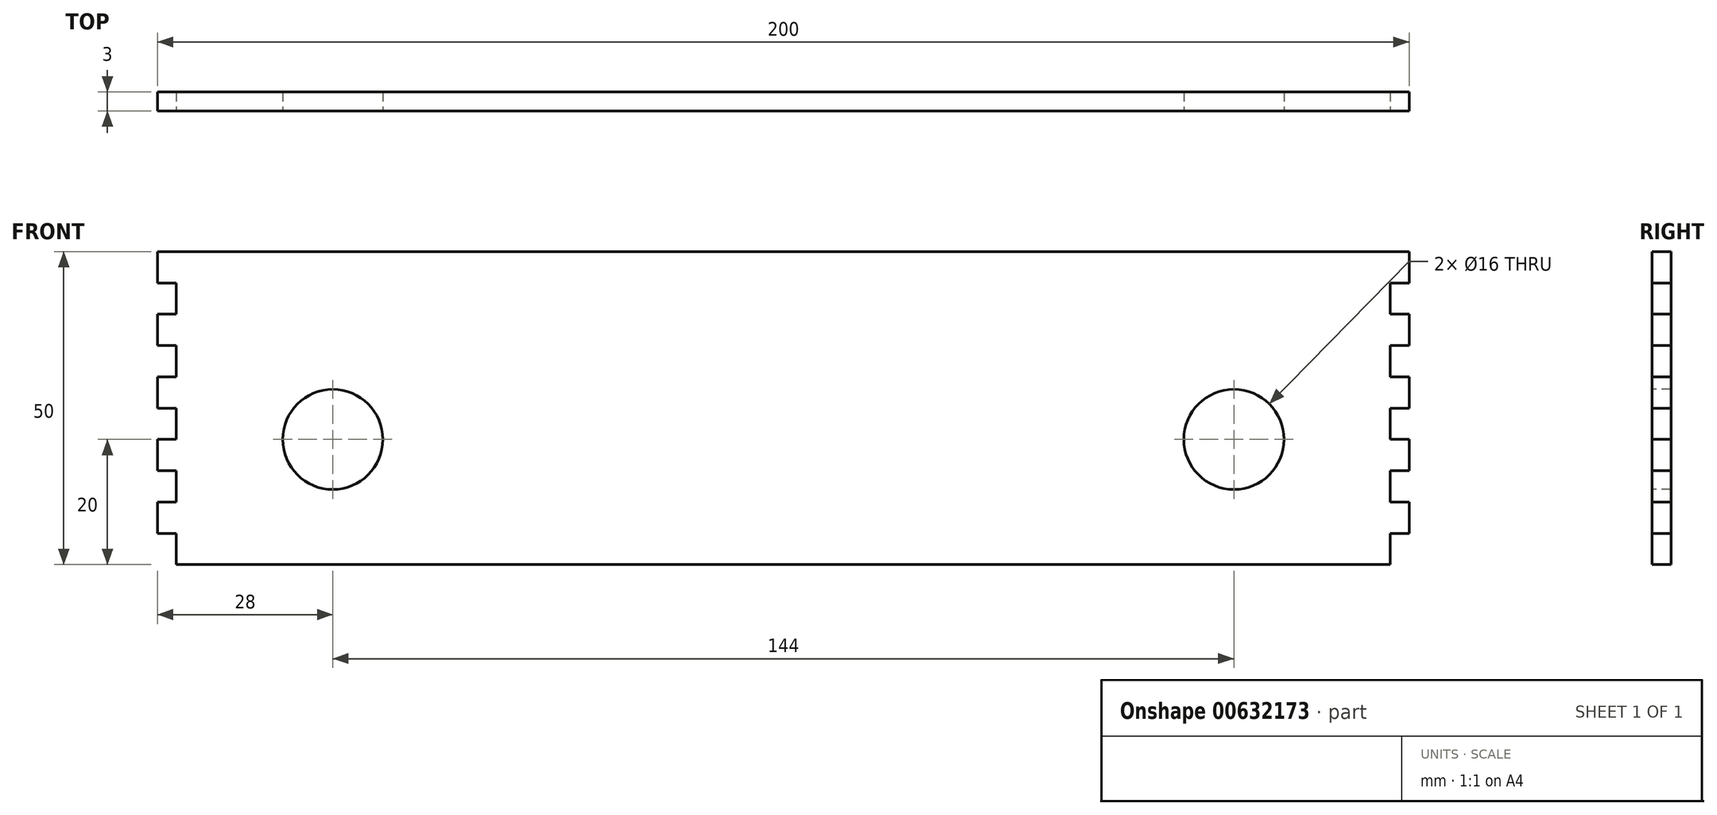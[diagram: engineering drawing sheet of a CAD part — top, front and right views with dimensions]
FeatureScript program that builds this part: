
annotation { "Feature Type Name" : "Feature", "Feature Type Description" : "" }
export const myFeature = defineFeature(function(context is Context, id is Id, definition is map)
    precondition{}
    {
        {
            var Q0;
            Q0=qCreatedBy(makeId("Front.planeOp"),FACE);
            var sketch = newSketch(context, id + "F0", { "sketchPlane" : qUnion([Q0])});
            skLineSegment(sketch, "E0.bottom", {"start": v(97, 25) * mm, "end": v(-97, 25) * mm});
            skLineSegment(sketch, "E0.top", {"start": v(97, -25) * mm, "end": v(-97, -25) * mm});
            skLineSegment(sketch, "E0.left", {"start": v(97, 25) * mm, "end": v(97, -25) * mm});
            skLineSegment(sketch, "E0.right", {"start": v(-97, 25) * mm, "end": v(-97, -25) * mm});
            skPoint(sketch, "E0.middle", {"position": v(0, 0) * mm});
            skSolve(sketch);
        }
        {
            var Q0;
            Q0=makeQuery(id+"F0.imprint","IMPRINT",FACE,{"disambiguationData":[TD([[makeQuery(id+"F0.imprint","IMPRINT",EDGE,{"derivedFrom":sQuery(id+"F0.wireOp",EDGE,"E0.bottom")}),1.0]])]});
            extrude(context, id + "F1", {"entities" : qUnion([Q0]), "depth" : 3 * mm, "offsetDistance" : 25 * mm});
        }
        {
            var Q0;
            Q0=makeQuery(id+"F1.opExtrude","CAP_FACE",FACE,{"disambiguationData":[OSD([sQuery(id+"F0.wireOp",EDGE,"E0.bottom"),sQuery(id+"F0.wireOp",EDGE,"E0.top"),sQuery(id+"F0.wireOp",EDGE,"E0.left"),sQuery(id+"F0.wireOp",EDGE,"E0.right")])],"isStart":false});
            var sketch = newSketch(context, id + "F2", { "sketchPlane" : qUnion([Q0])});
            skLineSegment(sketch, "E1.bottom", {"start": v(-97, 25) * mm, "end": v(-100, 25) * mm});
            skLineSegment(sketch, "E1.top", {"start": v(-97, 20) * mm, "end": v(-100, 20) * mm});
            skLineSegment(sketch, "E1.left", {"start": v(-97, 25) * mm, "end": v(-97, 20) * mm});
            skLineSegment(sketch, "E1.right", {"start": v(-100, 25) * mm, "end": v(-100, 20) * mm});
            skLineSegment(sketch, "E2.0.1.0", {"start": v(-97, 15) * mm, "end": v(-100, 15) * mm});
            skLineSegment(sketch, "E2.0.1.1", {"start": v(-97, 10) * mm, "end": v(-100, 10) * mm});
            skLineSegment(sketch, "E2.0.1.2", {"start": v(-97, 15) * mm, "end": v(-97, 10) * mm});
            skLineSegment(sketch, "E2.0.1.3", {"start": v(-100, 15) * mm, "end": v(-100, 10) * mm});
            skLineSegment(sketch, "E2.0.2.0", {"start": v(-97, 5) * mm, "end": v(-100, 5) * mm});
            skLineSegment(sketch, "E2.0.2.1", {"start": v(-97, 0) * mm, "end": v(-100, 0) * mm});
            skLineSegment(sketch, "E2.0.2.2", {"start": v(-97, 5) * mm, "end": v(-97, 0) * mm});
            skLineSegment(sketch, "E2.0.2.3", {"start": v(-100, 5) * mm, "end": v(-100, 0) * mm});
            skLineSegment(sketch, "E2.0.3.0", {"start": v(-97, -5) * mm, "end": v(-100, -5) * mm});
            skLineSegment(sketch, "E2.0.3.1", {"start": v(-97, -10) * mm, "end": v(-100, -10) * mm});
            skLineSegment(sketch, "E2.0.3.2", {"start": v(-97, -5) * mm, "end": v(-97, -10) * mm});
            skLineSegment(sketch, "E2.0.3.3", {"start": v(-100, -5) * mm, "end": v(-100, -10) * mm});
            skLineSegment(sketch, "E2.0.4.0", {"start": v(-97, -15) * mm, "end": v(-100, -15) * mm});
            skLineSegment(sketch, "E2.0.4.1", {"start": v(-97, -20) * mm, "end": v(-100, -20) * mm});
            skLineSegment(sketch, "E2.0.4.2", {"start": v(-97, -15) * mm, "end": v(-97, -20) * mm});
            skLineSegment(sketch, "E2.0.4.3", {"start": v(-100, -15) * mm, "end": v(-100, -20) * mm});
            skLineSegment(sketch, "E2.direction1", {"start": v(-100, 20) * mm, "end": v(-74.1, 20) * mm, "construction": true});
            skLineSegment(sketch, "E2.direction2", {"start": v(-100, 20) * mm, "end": v(-100, 10) * mm, "construction": true});
            skLineSegment(sketch, "E3.MirrorCS", {"start": v(97, 10) * mm, "end": v(100, 10) * mm});
            skLineSegment(sketch, "E4.MirrorCS", {"start": v(97, 15) * mm, "end": v(100, 15) * mm});
            skLineSegment(sketch, "E5.MirrorCS", {"start": v(100, 15) * mm, "end": v(100, 10) * mm});
            skLineSegment(sketch, "E6.MirrorCS", {"start": v(97, 15) * mm, "end": v(97, 10) * mm});
            skLineSegment(sketch, "E7.MirrorCS", {"start": v(97, 20) * mm, "end": v(100, 20) * mm});
            skLineSegment(sketch, "E8.MirrorCS", {"start": v(100, 20) * mm, "end": v(100, 10) * mm, "construction": true});
            skLineSegment(sketch, "E9.MirrorCS", {"start": v(97, 5) * mm, "end": v(100, 5) * mm});
            skLineSegment(sketch, "E10.MirrorCS", {"start": v(97, 0) * mm, "end": v(100, 0) * mm});
            skLineSegment(sketch, "E11.MirrorCS", {"start": v(100, 25) * mm, "end": v(100, 20) * mm});
            skLineSegment(sketch, "E12.MirrorCS", {"start": v(97, 25) * mm, "end": v(97, 20) * mm});
            skLineSegment(sketch, "E13.MirrorCS", {"start": v(97, 25) * mm, "end": v(100, 25) * mm});
            skLineSegment(sketch, "E14.MirrorCS", {"start": v(97, -10) * mm, "end": v(100, -10) * mm});
            skLineSegment(sketch, "E15.MirrorCS", {"start": v(97, -5) * mm, "end": v(100, -5) * mm});
            skLineSegment(sketch, "E16.MirrorCS", {"start": v(97, 5) * mm, "end": v(97, 0) * mm});
            skLineSegment(sketch, "E17.MirrorCS", {"start": v(100, -5) * mm, "end": v(100, -10) * mm});
            skLineSegment(sketch, "E18.MirrorCS", {"start": v(97, -5) * mm, "end": v(97, -10) * mm});
            skLineSegment(sketch, "E19.MirrorCS", {"start": v(97, -15) * mm, "end": v(100, -15) * mm});
            skLineSegment(sketch, "E20.MirrorCS", {"start": v(100, 5) * mm, "end": v(100, 0) * mm});
            skLineSegment(sketch, "E21.MirrorCS", {"start": v(97, -20) * mm, "end": v(100, -20) * mm});
            skLineSegment(sketch, "E22.MirrorCS", {"start": v(100, -15) * mm, "end": v(100, -20) * mm});
            skLineSegment(sketch, "E23.MirrorCS", {"start": v(97, -15) * mm, "end": v(97, -20) * mm});
            skSolve(sketch);
        }
        {
            var Q0;
            Q0 = qSketchRegion(id + "F2", true);
            extrude(context, id + "F3", {"entities" : qUnion([Q0]), "operationType" : NewBodyOperationType.ADD, "oppositeDirection" : true, "depth" : 3 * mm, "offsetDistance" : 25 * mm});
        }
        {
            var Q0;
            Q0=makeQuery(id+"F3.boolean.opBoolean","MERGE",FACE,{"derivedFrom":[makeQuery(id+"F1.opExtrude","CAP_FACE",FACE,{"disambiguationData":[OSD([sQuery(id+"F0.wireOp",EDGE,"E0.bottom"),sQuery(id+"F0.wireOp",EDGE,"E0.top"),sQuery(id+"F0.wireOp",EDGE,"E0.left"),sQuery(id+"F0.wireOp",EDGE,"E0.right")])],"isStart":false}),makeQuery(id+"F3.opExtrude","CAP_FACE",FACE,{"disambiguationData":[OSD([sQuery(id+"F2.wireOp",EDGE,"E1.bottom"),sQuery(id+"F2.wireOp",EDGE,"E1.top"),sQuery(id+"F2.wireOp",EDGE,"E1.left"),sQuery(id+"F2.wireOp",EDGE,"E1.right")])],"isStart":true}),makeQuery(id+"F3.opExtrude","CAP_FACE",FACE,{"disambiguationData":[OSD([sQuery(id+"F2.wireOp",EDGE,"E2.0.1.0"),sQuery(id+"F2.wireOp",EDGE,"E2.0.1.1"),sQuery(id+"F2.wireOp",EDGE,"E2.0.1.2"),sQuery(id+"F2.wireOp",EDGE,"E2.0.1.3")])],"isStart":true}),makeQuery(id+"F3.opExtrude","CAP_FACE",FACE,{"disambiguationData":[OSD([sQuery(id+"F2.wireOp",EDGE,"E2.0.2.0"),sQuery(id+"F2.wireOp",EDGE,"E2.0.2.1"),sQuery(id+"F2.wireOp",EDGE,"E2.0.2.2"),sQuery(id+"F2.wireOp",EDGE,"E2.0.2.3")])],"isStart":true}),makeQuery(id+"F3.opExtrude","CAP_FACE",FACE,{"disambiguationData":[OSD([sQuery(id+"F2.wireOp",EDGE,"E2.0.3.0"),sQuery(id+"F2.wireOp",EDGE,"E2.0.3.1"),sQuery(id+"F2.wireOp",EDGE,"E2.0.3.2"),sQuery(id+"F2.wireOp",EDGE,"E2.0.3.3")])],"isStart":true}),makeQuery(id+"F3.opExtrude","CAP_FACE",FACE,{"disambiguationData":[OSD([sQuery(id+"F2.wireOp",EDGE,"E2.0.4.0"),sQuery(id+"F2.wireOp",EDGE,"E2.0.4.1"),sQuery(id+"F2.wireOp",EDGE,"E2.0.4.2"),sQuery(id+"F2.wireOp",EDGE,"E2.0.4.3")])],"isStart":true}),makeQuery(id+"F3.opExtrude","CAP_FACE",FACE,{"disambiguationData":[OSD([sQuery(id+"F2.wireOp",EDGE,"E3.MirrorCS"),sQuery(id+"F2.wireOp",EDGE,"E4.MirrorCS"),sQuery(id+"F2.wireOp",EDGE,"E5.MirrorCS"),sQuery(id+"F2.wireOp",EDGE,"E6.MirrorCS")])],"isStart":true}),makeQuery(id+"F3.opExtrude","CAP_FACE",FACE,{"disambiguationData":[OSD([sQuery(id+"F2.wireOp",EDGE,"E7.MirrorCS"),sQuery(id+"F2.wireOp",EDGE,"E11.MirrorCS"),sQuery(id+"F2.wireOp",EDGE,"E12.MirrorCS"),sQuery(id+"F2.wireOp",EDGE,"E13.MirrorCS")])],"isStart":true}),makeQuery(id+"F3.opExtrude","CAP_FACE",FACE,{"disambiguationData":[OSD([sQuery(id+"F2.wireOp",EDGE,"E9.MirrorCS"),sQuery(id+"F2.wireOp",EDGE,"E10.MirrorCS"),sQuery(id+"F2.wireOp",EDGE,"E16.MirrorCS"),sQuery(id+"F2.wireOp",EDGE,"E20.MirrorCS")])],"isStart":true}),makeQuery(id+"F3.opExtrude","CAP_FACE",FACE,{"disambiguationData":[OSD([sQuery(id+"F2.wireOp",EDGE,"E14.MirrorCS"),sQuery(id+"F2.wireOp",EDGE,"E15.MirrorCS"),sQuery(id+"F2.wireOp",EDGE,"E17.MirrorCS"),sQuery(id+"F2.wireOp",EDGE,"E18.MirrorCS")])],"isStart":true}),makeQuery(id+"F3.opExtrude","CAP_FACE",FACE,{"disambiguationData":[OSD([sQuery(id+"F2.wireOp",EDGE,"E19.MirrorCS"),sQuery(id+"F2.wireOp",EDGE,"E21.MirrorCS"),sQuery(id+"F2.wireOp",EDGE,"E22.MirrorCS"),sQuery(id+"F2.wireOp",EDGE,"E23.MirrorCS")])],"isStart":true})]});
            var sketch = newSketch(context, id + "F4", { "sketchPlane" : qUnion([Q0])});
            skLineSegment(sketch, "E24", {"start": v(-100, 25) * mm, "end": v(-72, 25) * mm, "construction": true});
            skLineSegment(sketch, "E25", {"start": v(-72, 25) * mm, "end": v(-72, -5) * mm, "construction": true});
            skCircle(sketch, "E26", {"center": v(-72, -5) * mm, "radius": 8 * mm});
            skCircle(sketch, "E27.MirrorC", {"center": v(72, -5) * mm, "radius": 8 * mm});
            skSolve(sketch);
        }
        {
            var Q0;
            Q0 = qSketchRegion(id + "F4", true);
            extrude(context, id + "F5", {"entities" : qUnion([Q0]), "operationType" : NewBodyOperationType.REMOVE, "oppositeDirection" : true, "depth" : 25 * mm, "offsetDistance" : 25 * mm});
        }
    });
